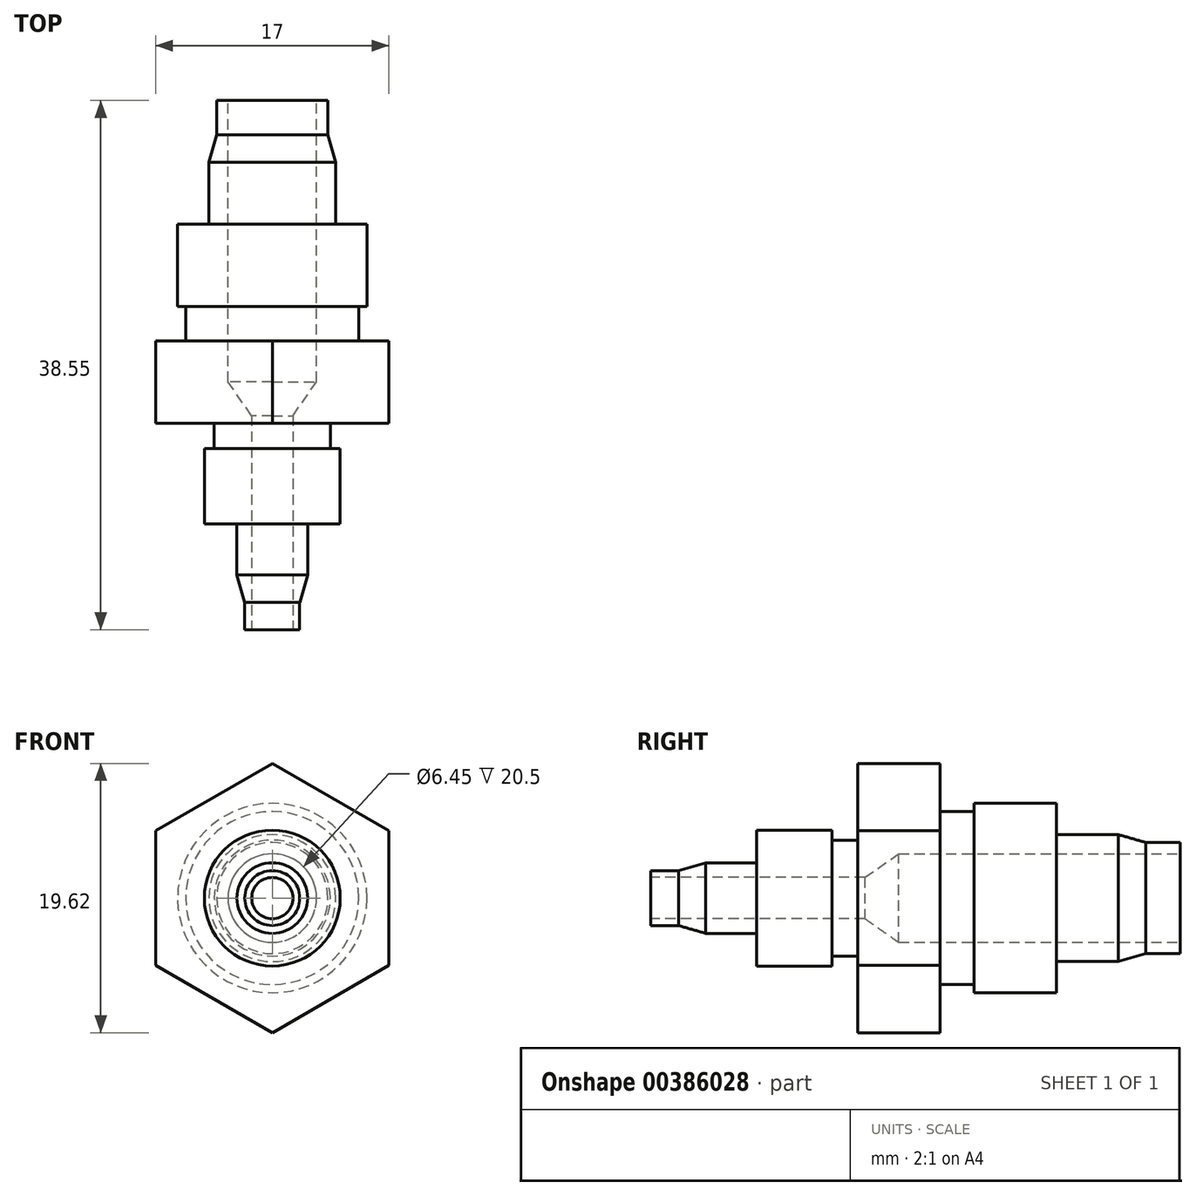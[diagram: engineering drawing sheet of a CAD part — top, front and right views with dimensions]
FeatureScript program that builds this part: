
annotation { "Feature Type Name" : "Feature", "Feature Type Description" : "" }
export const myFeature = defineFeature(function(context is Context, id is Id, definition is map)
    precondition{}
    {
        {
            var Q0;
            Q0=qCreatedBy(makeId("Front.planeOp"),FACE);
            var sketch = newSketch(context, id + "F0", { "sketchPlane" : qUnion([Q0])});
            skCircle(sketch, "E0.cCircle", {"center": v(0, 0) * mm, "radius": 9.81 * mm, "construction": true});
            skLineSegment(sketch, "E0.0", {"start": v(0, -9.81) * mm, "end": v(-8.5, -4.9) * mm});
            skLineSegment(sketch, "E0.1", {"start": v(-8.5, -4.9) * mm, "end": v(-8.5, 4.9) * mm});
            skLineSegment(sketch, "E0.2", {"start": v(-8.5, 4.9) * mm, "end": v(0, 9.81) * mm});
            skLineSegment(sketch, "E0.3", {"start": v(0, 9.81) * mm, "end": v(8.5, 4.9) * mm});
            skLineSegment(sketch, "E0.4", {"start": v(8.5, 4.9) * mm, "end": v(8.5, -4.9) * mm});
            skLineSegment(sketch, "E0.5", {"start": v(8.5, -4.9) * mm, "end": v(0, -9.81) * mm});
            skSolve(sketch);
        }
        {
            var Q0;
            Q0 = qSketchRegion(id + "F0", true);
            extrude(context, id + "F1", {"entities" : qUnion([Q0]), "endBound" : BoundingType.SYMMETRIC, "depth" : 6 * mm});
        }
        {
            var Q0;
            Q0=makeQuery(id+"F1.opExtrude","CAP_FACE",FACE,{"disambiguationData":[OSD([sQuery(id+"F0.wireOp",EDGE,"E0.0"),sQuery(id+"F0.wireOp",EDGE,"E0.1"),sQuery(id+"F0.wireOp",EDGE,"E0.2"),sQuery(id+"F0.wireOp",EDGE,"E0.3"),sQuery(id+"F0.wireOp",EDGE,"E0.4"),sQuery(id+"F0.wireOp",EDGE,"E0.5")])],"isStart":true});
            var sketch = newSketch(context, id + "F2", { "sketchPlane" : qUnion([Q0])});
            skCircle(sketch, "E1", {"center": v(0, 0) * mm, "radius": 6.3 * mm});
            skSolve(sketch);
        }
        {
            var Q0;
            Q0=makeQuery(id+"F2.imprint","IMPRINT",FACE,{"disambiguationData":[TD([[makeQuery(id+"F2.imprint","IMPRINT",EDGE,{"derivedFrom":sQuery(id+"F2.wireOp",EDGE,"E1")}),1.0]])]});
            extrude(context, id + "F3", {"entities" : qUnion([Q0]), "operationType" : NewBodyOperationType.ADD, "depth" : 2.5 * mm});
        }
        {
            var Q0;
            Q0=makeQuery(id+"F3.opExtrude","CAP_FACE",FACE,{"disambiguationData":[OSD([sQuery(id+"F2.wireOp",EDGE,"E1")])],"isStart":false});
            var sketch = newSketch(context, id + "F4", { "sketchPlane" : qUnion([Q0])});
            skCircle(sketch, "E2", {"center": v(0, 0) * mm, "radius": 6.9 * mm});
            skSolve(sketch);
        }
        {
            var Q0;
            Q0 = qSketchRegion(id + "F4", true);
            extrude(context, id + "F5", {"entities" : qUnion([Q0]), "operationType" : NewBodyOperationType.ADD, "depth" : 6 * mm});
        }
        {
            var Q0;
            Q0=makeQuery(id+"F5.opExtrude","CAP_FACE",FACE,{"disambiguationData":[OSD([sQuery(id+"F4.wireOp",EDGE,"E2")])],"isStart":false});
            var sketch = newSketch(context, id + "F6", { "sketchPlane" : qUnion([Q0])});
            skCircle(sketch, "E3", {"center": v(0, 0) * mm, "radius": 4.62 * mm});
            skSolve(sketch);
        }
        {
            var Q0;
            Q0=makeQuery(id+"F6.imprint","IMPRINT",FACE,{"disambiguationData":[TD([[makeQuery(id+"F6.imprint","IMPRINT",EDGE,{"derivedFrom":sQuery(id+"F6.wireOp",EDGE,"E3")}),1.0]])]});
            extrude(context, id + "F7", {"entities" : qUnion([Q0]), "operationType" : NewBodyOperationType.ADD, "depth" : 4.5 * mm});
        }
        {
            var Q0;
            Q0=makeQuery(id+"F7.opExtrude","CAP_FACE",FACE,{"disambiguationData":[OSD([sQuery(id+"F6.wireOp",EDGE,"E3")])],"isStart":false});
            var sketch = newSketch(context, id + "F8", { "sketchPlane" : qUnion([Q0])});
            skCircle(sketch, "E4", {"center": v(0, 0) * mm, "radius": 4.62 * mm});
            skSolve(sketch);
        }
        {
            var Q0;
            Q0 = qSketchRegion(id + "F8", true);
            extrude(context, id + "F9", {"entities" : qUnion([Q0]), "operationType" : NewBodyOperationType.ADD, "depth" : 2 * mm, "hasDraft" : true, "draftAngle" : 16 * degree, "draftPullDirection" : true});
        }
        {
            var Q0;
            Q0=makeQuery(id+"F9.opExtrude","CAP_FACE",FACE,{"disambiguationData":[OSD([sQuery(id+"F8.wireOp",EDGE,"E4")])],"isStart":false});
            var sketch = newSketch(context, id + "F10", { "sketchPlane" : qUnion([Q0])});
            skCircle(sketch, "E5", {"center": v(0, 0) * mm, "radius": 4 * mm});
            skSolve(sketch);
        }
        {
            var Q0;
            Q0=makeQuery(id+"F10.imprint","IMPRINT",FACE,{"disambiguationData":[TD([[makeQuery(id+"F10.imprint","IMPRINT",EDGE,{"derivedFrom":makeQuery(id+"F9.opExtrude","CAP_EDGE",EDGE,{"disambiguationData":[OSD([sQuery(id+"F8.wireOp",EDGE,"E4")])],"isStart":false})}),1.0]])]});
            var Q1;
            Q1=makeQuery(id+"F10.imprint","IMPRINT",FACE,{"disambiguationData":[TD([[makeQuery(id+"F10.imprint","IMPRINT",EDGE,{"derivedFrom":sQuery(id+"F10.wireOp",EDGE,"E5")}),1.0]])]});
            extrude(context, id + "F11", {"entities" : qUnion([Q0, Q1]), "operationType" : NewBodyOperationType.ADD, "depth" : 2.5 * mm});
        }
        {
            var Q0;
            Q0=makeQuery(id+"F11.opExtrude","CAP_FACE",FACE,{"disambiguationData":[OSD([sQuery(id+"F8.wireOp",EDGE,"E4")])],"isStart":false});
            var sketch = newSketch(context, id + "F12", { "sketchPlane" : qUnion([Q0])});
            skCircle(sketch, "E6", {"center": v(0, 0) * mm, "radius": 3.23 * mm});
            skSolve(sketch);
        }
        {
            var Q0;
            Q0=makeQuery(id+"F12.imprint","IMPRINT",FACE,{"disambiguationData":[TD([[makeQuery(id+"F12.imprint","IMPRINT",EDGE,{"derivedFrom":sQuery(id+"F12.wireOp",EDGE,"E6")}),1.0]])]});
            var Q1;
            Q1=qCreatedBy(makeId("Front.planeOp"),FACE);
            extrude(context, id + "F13", {"entities" : qUnion([Q0]), "operationType" : NewBodyOperationType.REMOVE, "endBound" : BoundingType.UP_TO_SURFACE, "oppositeDirection" : true, "endBoundEntityFace" : qUnion([Q1]), "depth" : 25 * mm});
        }
        {
            var Q0;
            Q0=makeQuery(id+"F1.opExtrude","CAP_FACE",FACE,{"disambiguationData":[OSD([sQuery(id+"F0.wireOp",EDGE,"E0.0"),sQuery(id+"F0.wireOp",EDGE,"E0.1"),sQuery(id+"F0.wireOp",EDGE,"E0.2"),sQuery(id+"F0.wireOp",EDGE,"E0.3"),sQuery(id+"F0.wireOp",EDGE,"E0.4"),sQuery(id+"F0.wireOp",EDGE,"E0.5")])],"isStart":false});
            var sketch = newSketch(context, id + "F14", { "sketchPlane" : qUnion([Q0])});
            skCircle(sketch, "E7", {"center": v(0, 0) * mm, "radius": 4.22 * mm});
            skSolve(sketch);
        }
        {
            var Q0;
            Q0 = qSketchRegion(id + "F14", true);
            extrude(context, id + "F15", {"entities" : qUnion([Q0]), "operationType" : NewBodyOperationType.ADD, "depth" : 1.85 * mm});
        }
        {
            var Q0;
            Q0=makeQuery(id+"F15.opExtrude","CAP_FACE",FACE,{"disambiguationData":[OSD([sQuery(id+"F14.wireOp",EDGE,"E7")])],"isStart":false});
            var sketch = newSketch(context, id + "F16", { "sketchPlane" : qUnion([Q0])});
            skCircle(sketch, "E8", {"center": v(0, 0) * mm, "radius": 4.95 * mm});
            skSolve(sketch);
        }
        {
            var Q0;
            Q0 = qSketchRegion(id + "F16", true);
            extrude(context, id + "F17", {"entities" : qUnion([Q0]), "operationType" : NewBodyOperationType.ADD, "depth" : 5.5 * mm});
        }
        {
            var Q0;
            Q0=makeQuery(id+"F17.opExtrude","CAP_FACE",FACE,{"disambiguationData":[OSD([sQuery(id+"F16.wireOp",EDGE,"E8")])],"isStart":false});
            var sketch = newSketch(context, id + "F18", { "sketchPlane" : qUnion([Q0])});
            skCircle(sketch, "E9", {"center": v(0, 0) * mm, "radius": 2.58 * mm});
            skSolve(sketch);
        }
        {
            var Q0;
            Q0=makeQuery(id+"F18.imprint","IMPRINT",FACE,{"disambiguationData":[TD([[makeQuery(id+"F18.imprint","IMPRINT",EDGE,{"derivedFrom":sQuery(id+"F18.wireOp",EDGE,"E9")}),1.0]])]});
            extrude(context, id + "F19", {"entities" : qUnion([Q0]), "operationType" : NewBodyOperationType.ADD, "depth" : 3.7 * mm});
        }
        {
            var Q0;
            Q0=makeQuery(id+"F19.opExtrude","CAP_FACE",FACE,{"disambiguationData":[OSD([sQuery(id+"F18.wireOp",EDGE,"E9")])],"isStart":false});
            var sketch = newSketch(context, id + "F20", { "sketchPlane" : qUnion([Q0])});
            skCircle(sketch, "E10", {"center": v(0, 0) * mm, "radius": 2.58 * mm});
            skSolve(sketch);
        }
        {
            var Q0;
            Q0 = qSketchRegion(id + "F20", true);
            extrude(context, id + "F21", {"entities" : qUnion([Q0]), "operationType" : NewBodyOperationType.ADD, "depth" : 2 * mm, "hasDraft" : true, "draftAngle" : 16 * degree, "draftPullDirection" : true});
        }
        {
            var Q0;
            Q0=makeQuery(id+"F21.opExtrude","CAP_FACE",FACE,{"disambiguationData":[OSD([sQuery(id+"F20.wireOp",EDGE,"E10")])],"isStart":false});
            var sketch = newSketch(context, id + "F22", { "sketchPlane" : qUnion([Q0])});
            skCircle(sketch, "E11", {"center": v(0, 0) * mm, "radius": 2 * mm});
            skSolve(sketch);
        }
        {
            var Q0;
            Q0=makeQuery(id+"F22.imprint","IMPRINT",FACE,{"disambiguationData":[TD([[makeQuery(id+"F22.imprint","IMPRINT",EDGE,{"derivedFrom":sQuery(id+"F22.wireOp",EDGE,"E11")}),1.0]])]});
            extrude(context, id + "F23", {"entities" : qUnion([Q0]), "operationType" : NewBodyOperationType.ADD, "depth" : 2 * mm});
        }
        {
            var Q0;
            Q0=makeQuery(id+"F23.opExtrude","CAP_FACE",FACE,{"disambiguationData":[OSD([sQuery(id+"F22.wireOp",EDGE,"E11")])],"isStart":false});
            var sketch = newSketch(context, id + "F24", { "sketchPlane" : qUnion([Q0])});
            skCircle(sketch, "E12", {"center": v(0, 0) * mm, "radius": 1.5 * mm});
            skSolve(sketch);
        }
        {
            var Q0;
            Q0=makeQuery(id+"F24.imprint","IMPRINT",FACE,{"disambiguationData":[TD([[makeQuery(id+"F24.imprint","IMPRINT",EDGE,{"derivedFrom":sQuery(id+"F24.wireOp",EDGE,"E12")}),1.0]])]});
            extrude(context, id + "F25", {"entities" : qUnion([Q0]), "operationType" : NewBodyOperationType.REMOVE, "endBound" : BoundingType.UP_TO_NEXT, "oppositeDirection" : true, "depth" : 25 * mm});
        }
        {
            var Q0;
            Q0=qCreatedBy(makeId("Front.planeOp"),FACE);
            var sketch = newSketch(context, id + "F26", { "sketchPlane" : qUnion([Q0])});
            skCircle(sketch, "E13", {"center": v(0, 0) * mm, "radius": 3.23 * mm});
            skSolve(sketch);
        }
        {
            var Q0;
            Q0 = qSketchRegion(id + "F26", true);
            extrude(context, id + "F27", {"entities" : qUnion([Q0]), "operationType" : NewBodyOperationType.REMOVE, "depth" : 3.5 * mm, "hasDraft" : true, "draftAngle" : 35 * degree, "draftPullDirection" : true});
        }
    });
